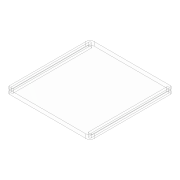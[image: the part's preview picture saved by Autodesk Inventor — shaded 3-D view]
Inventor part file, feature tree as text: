
AUTODESK INVENTOR PART (.ipt)
format: ipt  version: 2020 (Build 240168000, 168)  size: 139,264 bytes
history: native  units: mm
features: sketch x4, extrude x3, fillet x1, plane x1, mirror x1
ambient origin geometry x8: Origin, YZ Plane, XZ Plane, XY Plane, X Axis, Y Axis, Z Axis, Center Point
bodies: Solid1 (feature_tree)
feature tree (10):
  extrude  "Extrusion1"  Depth=105.0mm
  fillet  "Fillet1"  Radius=5.0mm
  sketch  "Sketch3"  dims[d10=5.0mm d11=2.5mm]
  extrude  "Extrusion3"  Depth=2.5mm
  extrude  "Extrusion4"  Depth=2.5mm
  plane  "Work Plane1"
  mirror  "Mirror1"
  sketch  "Sketch1"  dims[d0=105.0mm d1=105.0mm d2=5.0mm d3=0.0mm]
  sketch  "Sketch4"  dims[d12=2.5mm d13=2.5mm]
  sketch  "Sketch5"  dims[d14=2.5mm d15=4.0mm d16=4.0mm d17=4.0mm d18=4.0mm d19=3.0mm d20=3.0mm d21=3.0mm d22=3.0mm d23=10.0mm d24=0.0mm d25=10.0mm d26=0.0mm]
